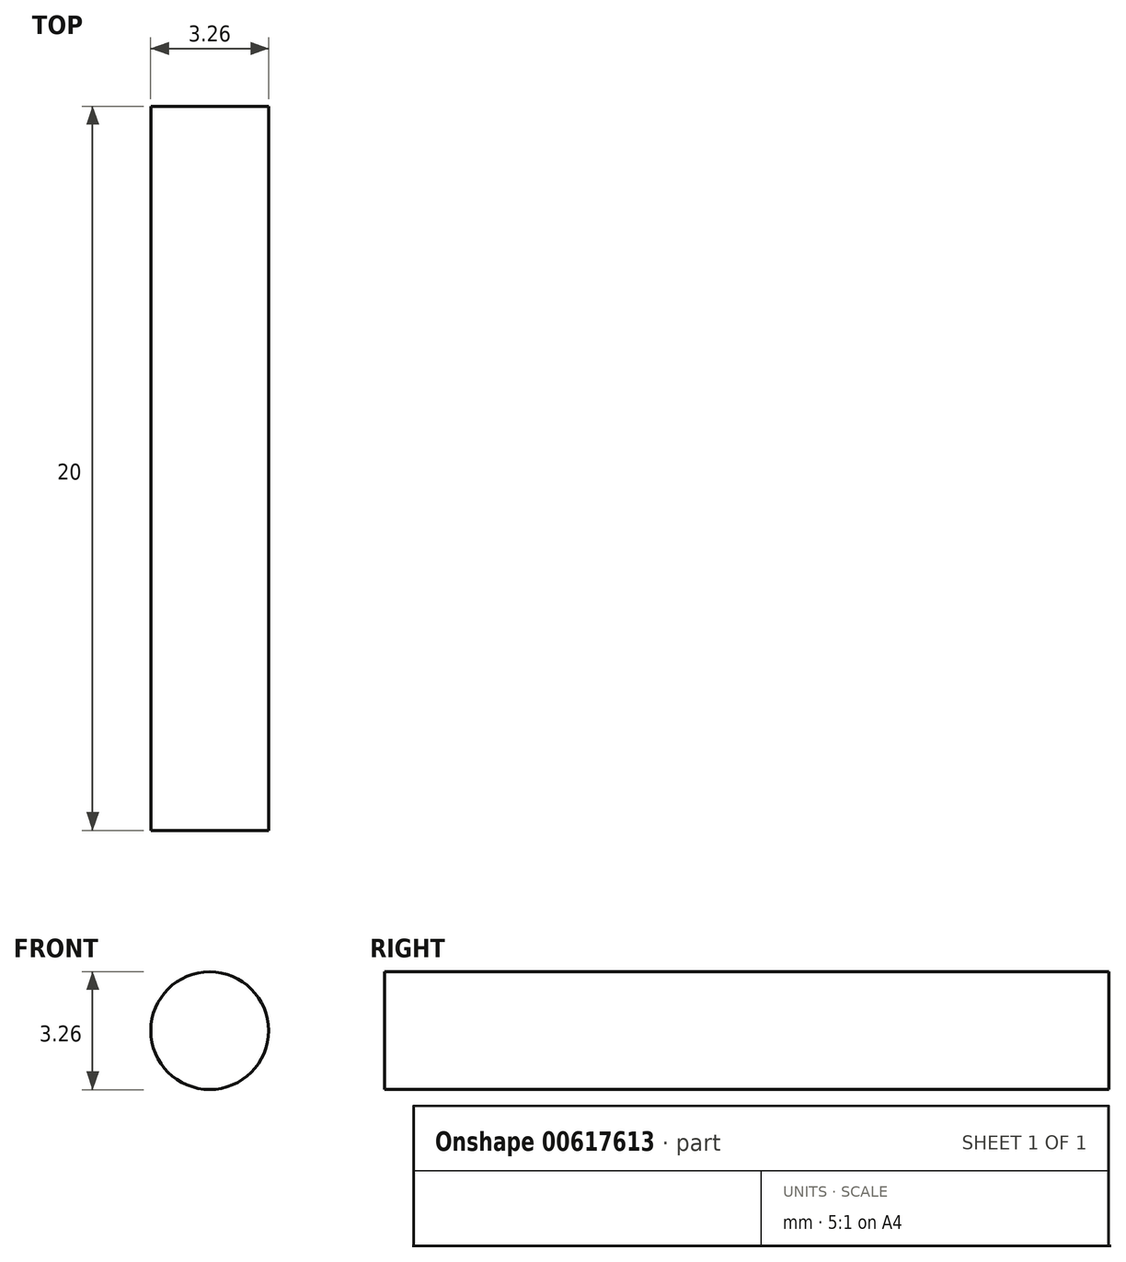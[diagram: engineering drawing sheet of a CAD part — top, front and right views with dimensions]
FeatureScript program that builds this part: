
annotation { "Feature Type Name" : "Feature", "Feature Type Description" : "" }
export const myFeature = defineFeature(function(context is Context, id is Id, definition is map)
    precondition{}
    {
        {
            var Q0;
            Q0=qCreatedBy(makeId("Front.planeOp"),FACE);
            var sketch = newSketch(context, id + "F0", { "sketchPlane" : qUnion([Q0])});
            skCircle(sketch, "E0", {"center": v(0, 0) * mm, "radius": 1.63 * mm});
            skSolve(sketch);
        }
        {
            var Q0;
            Q0=makeQuery(id+"F0.imprint","IMPRINT",FACE,{"disambiguationData":[TD([[makeQuery(id+"F0.imprint","IMPRINT",EDGE,{"derivedFrom":sQuery(id+"F0.wireOp",EDGE,"E0")}),1.0]])]});
            extrude(context, id + "F1", {"entities" : qUnion([Q0]), "depth" : 20 * mm, "offsetDistance" : 25 * mm});
        }
    });
